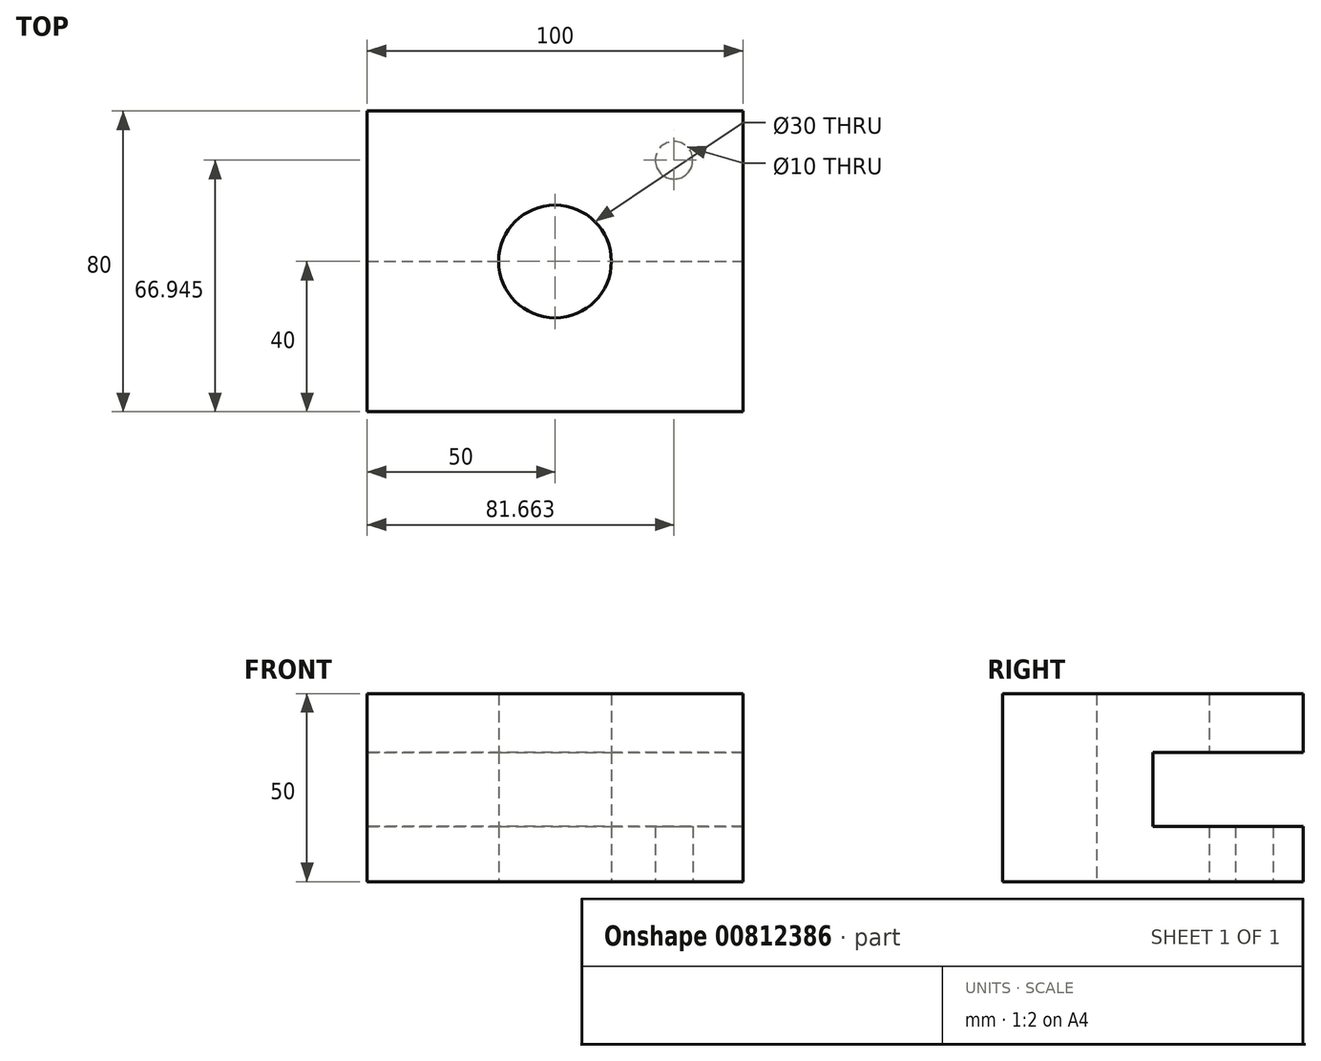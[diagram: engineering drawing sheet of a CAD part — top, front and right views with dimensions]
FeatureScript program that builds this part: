
annotation { "Feature Type Name" : "Feature", "Feature Type Description" : "" }
export const myFeature = defineFeature(function(context is Context, id is Id, definition is map)
    precondition{}
    {
        {
            var Q0;
            Q0=qCreatedBy(makeId("Top.planeOp"),FACE);
            var sketch = newSketch(context, id + "F0", { "sketchPlane" : qUnion([Q0])});
            skLineSegment(sketch, "E0.bottom", {"start": v(-50, 40) * mm, "end": v(50, 40) * mm});
            skLineSegment(sketch, "E0.top", {"start": v(-50, -40) * mm, "end": v(50, -40) * mm});
            skLineSegment(sketch, "E0.left", {"start": v(-50, 40) * mm, "end": v(-50, -40) * mm});
            skLineSegment(sketch, "E0.right", {"start": v(50, 40) * mm, "end": v(50, -40) * mm});
            skCircle(sketch, "E1", {"center": v(0, 0) * mm, "radius": 15 * mm});
            skSolve(sketch);
        }
        {
            var Q0;
            Q0 = qSketchRegion(id + "F0", true);
            extrude(context, id + "F1", {"entities" : qUnion([Q0]), "depth" : 50 * mm, "offsetDistance" : 25 * mm});
        }
        {
            var Q0;
            Q0=qCreatedBy(makeId("Front.planeOp"),FACE);
            var sketch = newSketch(context, id + "F2", { "sketchPlane" : qUnion([Q0])});
            skLineSegment(sketch, "E2.bottom", {"start": v(-63.81, 34.37) * mm, "end": v(68.3, 34.37) * mm});
            skLineSegment(sketch, "E2.top", {"start": v(-63.81, 14.64) * mm, "end": v(68.3, 14.64) * mm});
            skLineSegment(sketch, "E2.left", {"start": v(-63.81, 34.37) * mm, "end": v(-63.81, 14.64) * mm});
            skLineSegment(sketch, "E2.right", {"start": v(68.3, 34.37) * mm, "end": v(68.3, 14.64) * mm});
            skSolve(sketch);
        }
        {
            var Q0;
            Q0=makeQuery(id+"F2.imprint","IMPRINT",FACE,{"disambiguationData":[TD([[makeQuery(id+"F2.imprint","IMPRINT",EDGE,{"derivedFrom":sQuery(id+"F2.wireOp",EDGE,"E2.bottom")}),-1.0]])]});
            extrude(context, id + "F3", {"entities" : qUnion([Q0]), "operationType" : NewBodyOperationType.REMOVE, "oppositeDirection" : true, "depth" : 50 * mm, "offsetDistance" : 25 * mm});
        }
        {
            var Q0;
            Q0=qCreatedBy(makeId("Top.planeOp"),FACE);
            var sketch = newSketch(context, id + "F4", { "sketchPlane" : qUnion([Q0])});
            skCircle(sketch, "E3", {"center": v(31.66, 26.94) * mm, "radius": 5 * mm});
            skSolve(sketch);
        }
        {
            var Q0;
            Q0=makeQuery(id+"F4.imprint","IMPRINT",FACE,{"disambiguationData":[TD([[makeQuery(id+"F4.imprint","IMPRINT",EDGE,{"derivedFrom":sQuery(id+"F4.wireOp",EDGE,"E3")}),1.0]])]});
            var Q1;
            Q1=sQuery(id+"F4.wireOp",EDGE,"E3");
            extrude(context, id + "F5", {"entities" : qUnion([Q0]), "operationType" : NewBodyOperationType.REMOVE, "surfaceEntities" : qUnion([Q1]), "depth" : 25 * mm, "offsetDistance" : 25 * mm});
        }
    });
